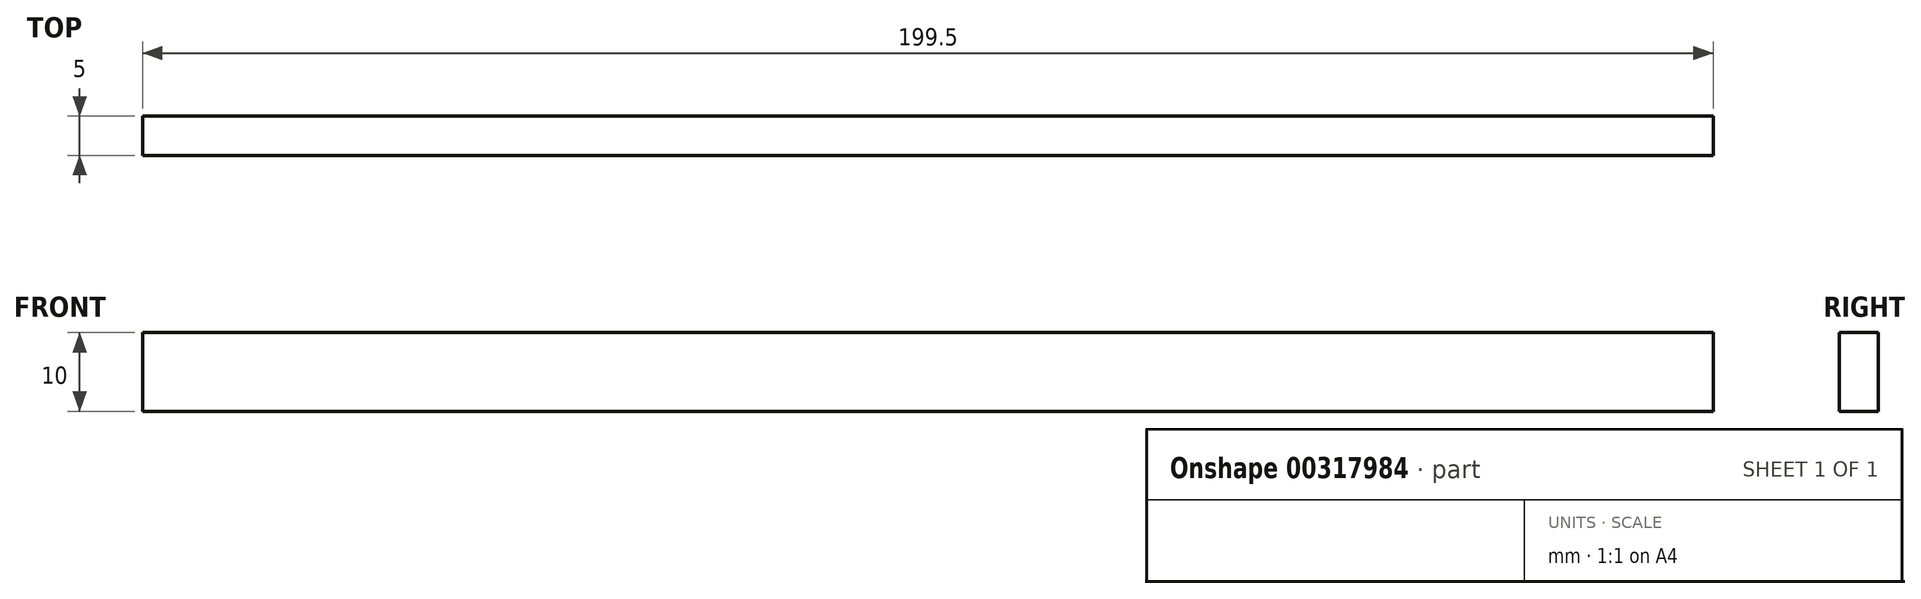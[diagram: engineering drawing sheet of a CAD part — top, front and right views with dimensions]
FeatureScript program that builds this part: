
annotation { "Feature Type Name" : "Feature", "Feature Type Description" : "" }
export const myFeature = defineFeature(function(context is Context, id is Id, definition is map)
    precondition{}
    {
        {
            var Q0;
            Q0=qCreatedBy(makeId("Front.planeOp"),FACE);
            var sketch = newSketch(context, id + "F0", { "sketchPlane" : qUnion([Q0])});
            skLineSegment(sketch, "E0.bottom", {"start": v(-99.75, 5) * mm, "end": v(99.75, 5) * mm});
            skLineSegment(sketch, "E0.top", {"start": v(-99.75, -5) * mm, "end": v(99.75, -5) * mm});
            skLineSegment(sketch, "E0.left", {"start": v(-99.75, 5) * mm, "end": v(-99.75, -5) * mm});
            skLineSegment(sketch, "E0.right", {"start": v(99.75, 5) * mm, "end": v(99.75, -5) * mm});
            skPoint(sketch, "E0.middle", {"position": v(0, 0) * mm});
            skSolve(sketch);
        }
        {
            var Q0;
            Q0=makeQuery(id+"F0.imprint","IMPRINT",FACE,{"disambiguationData":[TD([[makeQuery(id+"F0.imprint","IMPRINT",EDGE,{"derivedFrom":sQuery(id+"F0.wireOp",EDGE,"E0.bottom")}),-1.0]])]});
            extrude(context, id + "F1", {"entities" : qUnion([Q0]), "depth" : 5 * mm});
        }
    });
